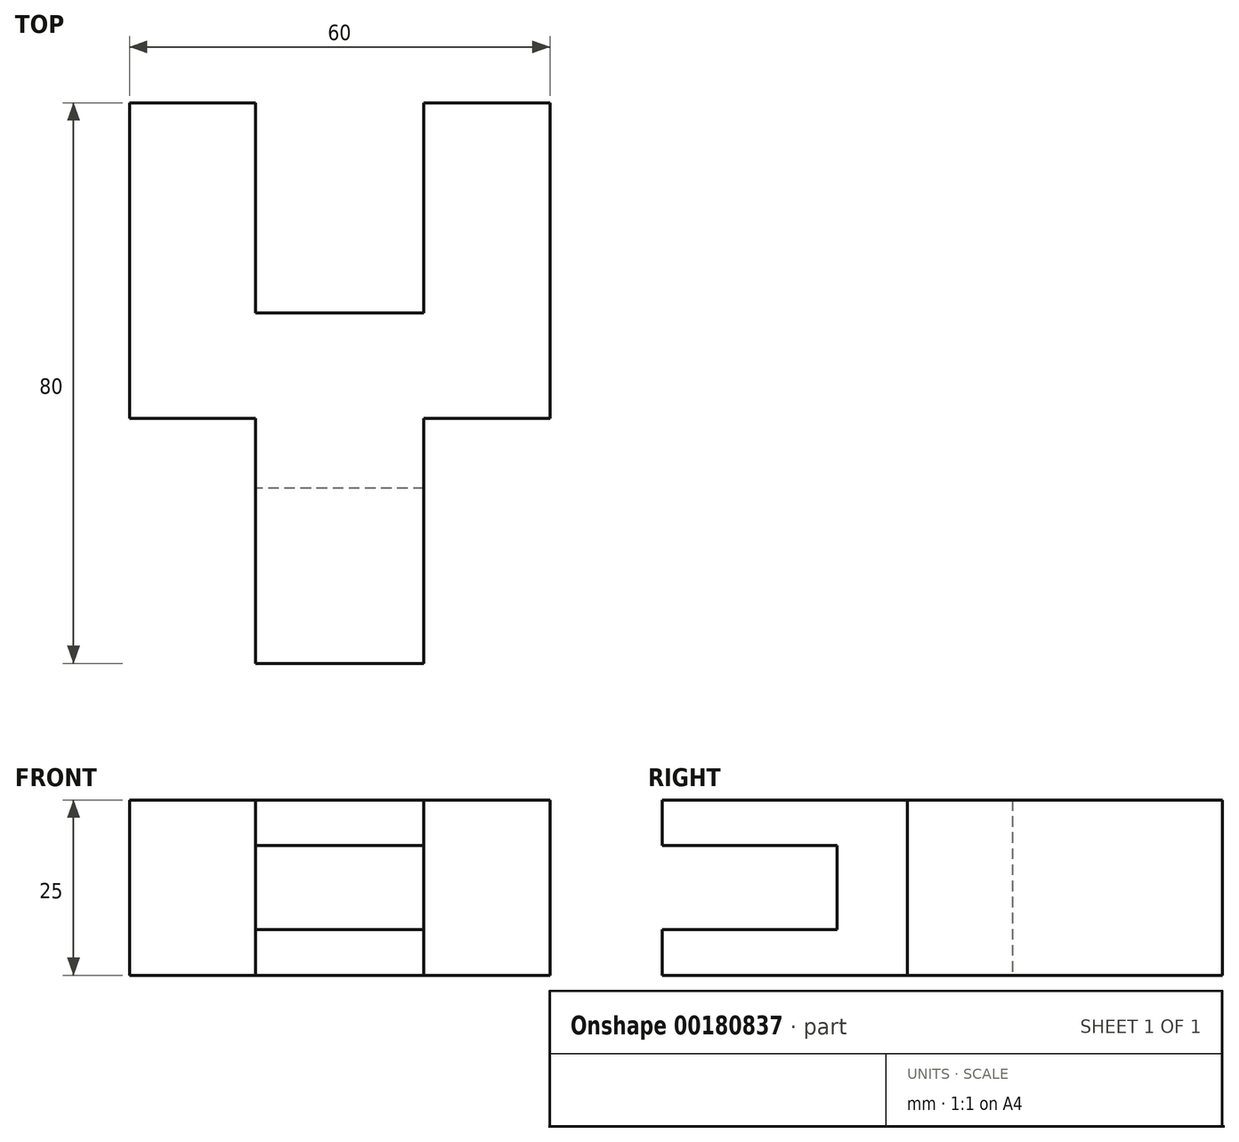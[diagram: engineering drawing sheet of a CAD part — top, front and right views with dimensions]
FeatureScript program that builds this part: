
annotation { "Feature Type Name" : "Feature", "Feature Type Description" : "" }
export const myFeature = defineFeature(function(context is Context, id is Id, definition is map)
    precondition{}
    {
        {
            var Q0;
            Q0=qCreatedBy(makeId("Top.planeOp"),FACE);
            var sketch = newSketch(context, id + "F0", { "sketchPlane" : qUnion([Q0])});
            skLineSegment(sketch, "E0", {"start": v(0, 0) * mm, "end": v(0, 45) * mm});
            skLineSegment(sketch, "E1", {"start": v(0, 45) * mm, "end": v(18, 45) * mm});
            skLineSegment(sketch, "E2", {"start": v(18, 45) * mm, "end": v(18, 15) * mm});
            skLineSegment(sketch, "E3", {"start": v(18, 15) * mm, "end": v(42, 15) * mm});
            skLineSegment(sketch, "E4", {"start": v(42, 15) * mm, "end": v(42, 45) * mm});
            skLineSegment(sketch, "E5", {"start": v(42, 45) * mm, "end": v(60, 45) * mm});
            skLineSegment(sketch, "E6", {"start": v(60, 45) * mm, "end": v(60, 0) * mm});
            skLineSegment(sketch, "E7", {"start": v(60, 0) * mm, "end": v(42, 0) * mm});
            skLineSegment(sketch, "E8", {"start": v(42, 0) * mm, "end": v(42, -35) * mm});
            skLineSegment(sketch, "E9", {"start": v(42, -35) * mm, "end": v(18, -35) * mm});
            skLineSegment(sketch, "E10", {"start": v(18, -35) * mm, "end": v(18, 0) * mm});
            skLineSegment(sketch, "E11", {"start": v(18, 0) * mm, "end": v(0, 0) * mm});
            skSolve(sketch);
        }
        {
            var Q0;
            Q0 = qSketchRegion(id + "F0", true);
            extrude(context, id + "F1", {"entities" : qUnion([Q0]), "depth" : 25 * mm});
        }
        {
            var Q0;
            Q0=qCreatedBy(makeId("Right.planeOp"),FACE);
            var sketch = newSketch(context, id + "F2", { "sketchPlane" : qUnion([Q0])});
            skLineSegment(sketch, "E12", {"start": v(-35, 18.5) * mm, "end": v(-10, 18.5) * mm});
            skLineSegment(sketch, "E13", {"start": v(-10, 18.5) * mm, "end": v(-10, 6.5) * mm});
            skLineSegment(sketch, "E14", {"start": v(-10, 6.5) * mm, "end": v(-35, 6.5) * mm});
            skLineSegment(sketch, "E15", {"start": v(-35, 6.5) * mm, "end": v(-35, 18.5) * mm});
            skSolve(sketch);
        }
        {
            var Q0;
            Q0 = qSketchRegion(id + "F2", true);
            extrude(context, id + "F3", {"entities" : qUnion([Q0]), "operationType" : NewBodyOperationType.REMOVE, "endBound" : BoundingType.THROUGH_ALL, "depth" : 25 * mm});
        }
    });
